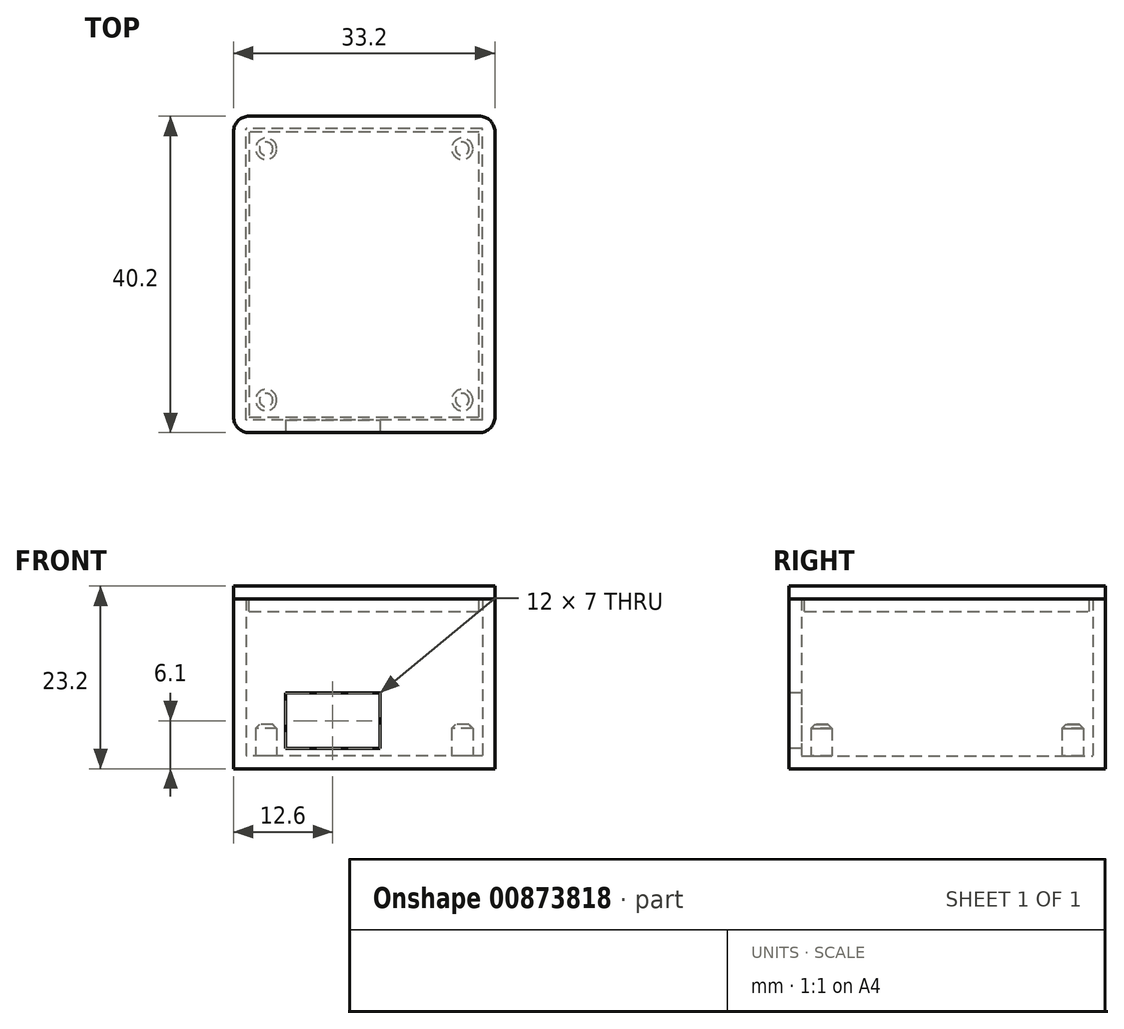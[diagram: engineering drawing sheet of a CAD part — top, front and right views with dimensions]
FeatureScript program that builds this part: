
annotation { "Feature Type Name" : "Feature", "Feature Type Description" : "" }
export const myFeature = defineFeature(function(context is Context, id is Id, definition is map)
    precondition{}
    {
        {
            var Q0;
            Q0=qCreatedBy(makeId("Top.planeOp"),FACE);
            var sketch = newSketch(context, id + "F0", { "sketchPlane" : qUnion([Q0])});
            skLineSegment(sketch, "E0.bottom", {"start": v(15, -18.5) * mm, "end": v(-15, -18.5) * mm});
            skLineSegment(sketch, "E0.top", {"start": v(15, 18.5) * mm, "end": v(-15, 18.5) * mm});
            skLineSegment(sketch, "E0.left", {"start": v(15, -18.5) * mm, "end": v(15, 18.5) * mm});
            skLineSegment(sketch, "E0.right", {"start": v(-15, -18.5) * mm, "end": v(-15, 18.5) * mm});
            skPoint(sketch, "E0.middle", {"position": v(0, 0) * mm});
            skLineSegment(sketch, "E1.0", {"start": v(16.6, 20.1) * mm, "end": v(-16.6, 20.1) * mm});
            skLineSegment(sketch, "E1.1", {"start": v(16.6, -20.1) * mm, "end": v(16.6, 20.1) * mm});
            skLineSegment(sketch, "E1.2", {"start": v(16.6, -20.1) * mm, "end": v(-16.6, -20.1) * mm});
            skLineSegment(sketch, "E1.3", {"start": v(-16.6, -20.1) * mm, "end": v(-16.6, 20.1) * mm});
            skSolve(sketch);
        }
        {
            var Q0;
            Q0 = qSketchRegion(id + "F0", true);
            extrude(context, id + "F1", {"entities" : qUnion([Q0]), "depth" : 20 * mm, "offsetDistance" : 25 * mm, "hasSecondDirection" : true, "secondDirectionOppositeDirection" : true, "secondDirectionDepth" : 1.6 * mm});
        }
        {
            var Q0;
            Q0=makeQuery(id+"F0.imprint","IMPRINT",FACE,{"disambiguationData":[TD([[makeQuery(id+"F0.imprint","IMPRINT",EDGE,{"derivedFrom":sQuery(id+"F0.wireOp",EDGE,"E0.bottom")}),-1.0]])]});
            extrude(context, id + "F2", {"entities" : qUnion([Q0]), "operationType" : NewBodyOperationType.ADD, "oppositeDirection" : true, "depth" : 1.6 * mm, "offsetDistance" : 25 * mm});
        }
        {
            var Q0;
            Q0=makeQuery(id+"F0.imprint","IMPRINT",FACE,{"disambiguationData":[TD([[makeQuery(id+"F0.imprint","IMPRINT",EDGE,{"derivedFrom":sQuery(id+"F0.wireOp",EDGE,"E0.bottom")}),-1.0]])]});
            var sketch = newSketch(context, id + "F3", { "sketchPlane" : qUnion([Q0])});
            skCircle(sketch, "E2", {"center": v(12.46, 15.96) * mm, "radius": 1.35 * mm});
            skCircle(sketch, "E3", {"center": v(12.46, -15.96) * mm, "radius": 1.35 * mm});
            skCircle(sketch, "E4", {"center": v(-12.46, -15.96) * mm, "radius": 1.35 * mm});
            skCircle(sketch, "E5", {"center": v(-12.46, 15.96) * mm, "radius": 1.35 * mm});
            skSolve(sketch);
        }
        {
            var Q0;
            Q0 = qSketchRegion(id + "F3", true);
            extrude(context, id + "F4", {"entities" : qUnion([Q0]), "operationType" : NewBodyOperationType.ADD, "depth" : 4 * mm, "offsetDistance" : 25 * mm});
        }
        {
            var Q0;
            Q0=makeQuery(id+"F4.opExtrude","CAP_FACE",FACE,{"disambiguationData":[OSD([sQuery(id+"F3.wireOp",EDGE,"E5")])],"isStart":false});
            var Q1;
            Q1=makeQuery(id+"F4.opExtrude","CAP_FACE",FACE,{"disambiguationData":[OSD([sQuery(id+"F3.wireOp",EDGE,"E2")])],"isStart":false});
            var Q2;
            Q2=makeQuery(id+"F4.opExtrude","CAP_FACE",FACE,{"disambiguationData":[OSD([sQuery(id+"F3.wireOp",EDGE,"E3")])],"isStart":false});
            var Q3;
            Q3=makeQuery(id+"F4.opExtrude","CAP_FACE",FACE,{"disambiguationData":[OSD([sQuery(id+"F3.wireOp",EDGE,"E4")])],"isStart":false});
            chamfer(context, id + "F5", {"entities" : qUnion([Q0, Q1, Q2, Q3]), "width" : .5 * mm, "tangentPropagation" : true});
        }
        {
            var Q0;
            Q0=makeQuery(id+"F1.opExtrude","CAP_FACE",FACE,{"disambiguationData":[OSD([sQuery(id+"F0.wireOp",EDGE,"E0.bottom"),sQuery(id+"F0.wireOp",EDGE,"E0.top"),sQuery(id+"F0.wireOp",EDGE,"E0.left"),sQuery(id+"F0.wireOp",EDGE,"E0.right"),sQuery(id+"F0.wireOp",EDGE,"E1.0"),sQuery(id+"F0.wireOp",EDGE,"E1.1"),sQuery(id+"F0.wireOp",EDGE,"E1.2"),sQuery(id+"F0.wireOp",EDGE,"E1.3")])],"isStart":false});
            var sketch = newSketch(context, id + "F6", { "sketchPlane" : qUnion([Q0])});
            skSolve(sketch);
        }
        {
            var Q0;
            Q0=makeQuery(id+"F6.imprint","IMPRINT",FACE,{"disambiguationData":[TD([[makeQuery(id+"F6.imprint","IMPRINT",EDGE,{"derivedFrom":makeQuery(id+"F1.opExtrude","CAP_EDGE",EDGE,{"disambiguationData":[OSD([sQuery(id+"F0.wireOp",EDGE,"E0.bottom")])],"isStart":false})}),-1.0]])]});
            var Q1;
            Q1=makeQuery(id+"F6.imprint","IMPRINT",FACE,{"disambiguationData":[TD([[makeQuery(id+"F6.imprint","IMPRINT",EDGE,{"derivedFrom":makeQuery(id+"F1.opExtrude","CAP_EDGE",EDGE,{"disambiguationData":[OSD([sQuery(id+"F0.wireOp",EDGE,"E0.bottom")])],"isStart":false})}),1.0]])]});
            extrude(context, id + "F7", {"entities" : qUnion([Q0, Q1]), "depth" : 1.6 * mm, "offsetDistance" : 25 * mm});
        }
        {
            var Q0;
            Q0=makeQuery(id+"F7.opExtrude","CAP_FACE",FACE,{"disambiguationData":[OSD([sQuery(id+"F0.wireOp",EDGE,"E1.0"),sQuery(id+"F0.wireOp",EDGE,"E1.1"),sQuery(id+"F0.wireOp",EDGE,"E1.2"),sQuery(id+"F0.wireOp",EDGE,"E1.3")])],"isStart":true});
            var sketch = newSketch(context, id + "F8", { "sketchPlane" : qUnion([Q0])});
            skLineSegment(sketch, "E6.0", {"start": v(14.6, 18.1) * mm, "end": v(14.6, -18.1) * mm});
            skLineSegment(sketch, "E6.1", {"start": v(-14.6, 18.1) * mm, "end": v(14.6, 18.1) * mm});
            skLineSegment(sketch, "E6.2", {"start": v(-14.6, -18.1) * mm, "end": v(-14.6, 18.1) * mm});
            skLineSegment(sketch, "E6.3", {"start": v(14.6, -18.1) * mm, "end": v(-14.6, -18.1) * mm});
            skSolve(sketch);
        }
        {
            var Q0;
            Q0 = qSketchRegion(id + "F8", true);
            extrude(context, id + "F9", {"entities" : qUnion([Q0]), "operationType" : NewBodyOperationType.ADD, "depth" : 1.6 * mm, "offsetDistance" : 25 * mm});
        }
        {
            var Q0;
            Q0=makeQuery(id+"F1.opExtrude","SWEPT_FACE",FACE,{"disambiguationData":[OSD([sQuery(id+"F0.wireOp",EDGE,"E1.2")])]});
            var sketch = newSketch(context, id + "F10", { "sketchPlane" : qUnion([Q0])});
            skLineSegment(sketch, "E7.bottom", {"start": v(2, 1) * mm, "end": v(-10, 1) * mm});
            skLineSegment(sketch, "E7.top", {"start": v(2, 8) * mm, "end": v(-10, 8) * mm});
            skLineSegment(sketch, "E7.left", {"start": v(2, 1) * mm, "end": v(2, 8) * mm});
            skLineSegment(sketch, "E7.right", {"start": v(-10, 1) * mm, "end": v(-10, 8) * mm});
            skPoint(sketch, "E7.middle", {"position": v(-4, 4.5) * mm});
            skSolve(sketch);
        }
        {
            var Q0;
            Q0 = qSketchRegion(id + "F10", true);
            extrude(context, id + "F11", {"entities" : qUnion([Q0]), "operationType" : NewBodyOperationType.REMOVE, "endBound" : BoundingType.UP_TO_NEXT, "oppositeDirection" : true, "depth" : 25 * mm, "offsetDistance" : 25 * mm});
        }
        {
            var Q0;
            Q0=makeQuery(id+"F1.opExtrude","SWEPT_EDGE",EDGE,{"disambiguationData":[OSD([sQuery(id+"F0.wireOp",EDGE,"E1.1"),sQuery(id+"F0.wireOp",EDGE,"E1.2")])]});
            var Q1;
            Q1=makeQuery(id+"F7.opExtrude","SWEPT_EDGE",EDGE,{"disambiguationData":[OSD([sQuery(id+"F0.wireOp",EDGE,"E1.1"),sQuery(id+"F0.wireOp",EDGE,"E1.2")])]});
            var Q2;
            Q2=makeQuery(id+"F1.opExtrude","SWEPT_EDGE",EDGE,{"disambiguationData":[OSD([sQuery(id+"F0.wireOp",EDGE,"E1.0"),sQuery(id+"F0.wireOp",EDGE,"E1.1")])]});
            var Q3;
            Q3=makeQuery(id+"F1.opExtrude","SWEPT_EDGE",EDGE,{"disambiguationData":[OSD([sQuery(id+"F0.wireOp",EDGE,"E1.0"),sQuery(id+"F0.wireOp",EDGE,"E1.3")])]});
            var Q4;
            Q4=makeQuery(id+"F7.opExtrude","SWEPT_EDGE",EDGE,{"disambiguationData":[OSD([sQuery(id+"F0.wireOp",EDGE,"E1.0"),sQuery(id+"F0.wireOp",EDGE,"E1.3")])]});
            var Q5;
            Q5=makeQuery(id+"F7.opExtrude","SWEPT_EDGE",EDGE,{"disambiguationData":[OSD([sQuery(id+"F0.wireOp",EDGE,"E1.0"),sQuery(id+"F0.wireOp",EDGE,"E1.1")])]});
            var Q6;
            Q6=makeQuery(id+"F1.opExtrude","SWEPT_EDGE",EDGE,{"disambiguationData":[OSD([sQuery(id+"F0.wireOp",EDGE,"E1.2"),sQuery(id+"F0.wireOp",EDGE,"E1.3")])]});
            var Q7;
            Q7=makeQuery(id+"F7.opExtrude","SWEPT_EDGE",EDGE,{"disambiguationData":[OSD([sQuery(id+"F0.wireOp",EDGE,"E1.2"),sQuery(id+"F0.wireOp",EDGE,"E1.3")])]});
            fillet(context, id + "F12", {"entities" : qUnion([Q0, Q1, Q2, Q3, Q4, Q5, Q6, Q7]), "radius" : 2 * mm, "tangentPropagation" : true, "allowEdgeOverflow" : false});
        }
    });
